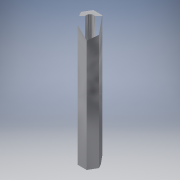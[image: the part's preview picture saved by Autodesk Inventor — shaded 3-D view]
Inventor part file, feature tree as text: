
AUTODESK INVENTOR PART (.ipt)
format: ipt  version: 2016 (Build 200138000, 138)  size: 115,200 bytes
history: native  units: in
note: dims shown in document units (in); Inventor stores cm internally (conversion verified against a paired STEP export)
features: extrude x1, sketch x1
ambient origin geometry x8: Origin, YZ Plane, XZ Plane, XY Plane, X Axis, Y Axis, Z Axis, Center Point
bodies: Solid1 (feature_tree)
feature tree (2):
  extrude  "Extrusion1"  Depth=4.0in
  sketch  "Sketch1"  dims[d0=0.231in d1=0.2475in d2=4.0in d3=0.0in]
